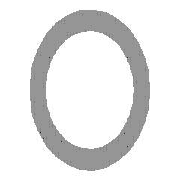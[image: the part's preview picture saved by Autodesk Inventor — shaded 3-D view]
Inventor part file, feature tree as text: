
AUTODESK INVENTOR PART (.ipt)
format: ipt  version: 2021 (Build 250183000, 183)  size: 752,128 bytes
history: native  units: mm (DEFAULTED — no unit token found)
features: other x19, plane x5, sketch x3, sweep x1, split x1
ambient origin geometry x8: Origin, YZ Plane, XZ Plane, XY Plane, X Axis, Y Axis, Z Axis, Center Point
bodies: Solid1 (feature_tree)
feature tree (29):
  parser-record x3  (decoder bookkeeping rows leaked as tree rows — omitted from the tree; the rows remain in map.json)
  other  "Driven Length"
  other  "Plano inicial"
  other  "Plano final"
  other  "Trayectoria de barrido"
  plane  "Plano de trabajo de orientación"
  sweep  "Cuerpo"
  plane  "Plano de trabajo5"
  split  "Dividir1"
  plane  "Plano de trabajo6"
  plane  "Plano de trabajo7"
  sketch  "Sketch3"  dims[d0=26.67mm d1=2.8702mm]
  plane  "Work Plane3"
  sketch  "Sketch4"  dims[d4=-0.0mm]
  sketch  "Boceto5"  dims[d5=1154.403192mm d6=90.0deg d7=1154.403192mm d8=0.0mm d9=0.0mm d18=0.0mm d19=90.0deg d20=0.0mm d21=90.0deg d54=5.0mm d55=0.0mm d56=5.0mm d57=0.0mm]
  other  "Sup7"
  other  "Sup33"
  other  "Sup34"
  other  "Sólido12"
  other  "SuperficieSolevación1"
  other  "Sup32"
  other  "Superficie de contorno21"
  other  "Superficie de contorno22"
  other  "Estructura 1617045494032.iam"
  other  "ANSI  1617061763005:1"
  other  "Marco_Bicicleta.iam"
  other  "Esqueleto_estructura:1"
note: 2 file-system paths scrubbed to <path> (originals preserved in map.json)
